# Revit family: FU_Stool_Sandler_Momo
name_source: partatom
category: Furniture
units: mm (PartAtom-declared; Revit-internal decimal feet)

## family parameters
Always vertical = Yes
Cut with Voids When Loaded = No
OmniClass Number = 23.40.20.00
OmniClass Title = General Furniture and Specialties
Room Calculation Point = No
Shared = No
Work Plane-Based = No

## types (1)
- Momo 3
    Arms_IsVisible = Yes
    Default Elevation = 0 mm  [stored 0 ft]
    Depth = 580 mm  [stored 1.90289 ft]
    Description = High stool with 4 legs made of expanded metal mesh welded to a curved tubular galvanised steel frame, polyester powder coated. Suitable for outdoor use as well as indoor. Stackable up to 6 units. Minimum order quantity 4 and only available in Multiples of 4
    Frame = Metal - Powdercoat - Black NCS 9000-N
    Height = 1100 mm  [stored 3.60892 ft]
    Manufacturer = Sandler
    Model = Momo 3
    Momo Mesh = Metal - Mesh - Black NCS 9000-N
    URL = https://www.sandlerseating.com
    Width = 540 mm  [stored 1.77165 ft]

note: [stored X ft] marks values corroborated as IEEE doubles in the binary element streams (Revit-internal decimal feet)

## geometry (parser evidence)
native form markers: Sweep x4
no freeform markers — native parametric forms only
